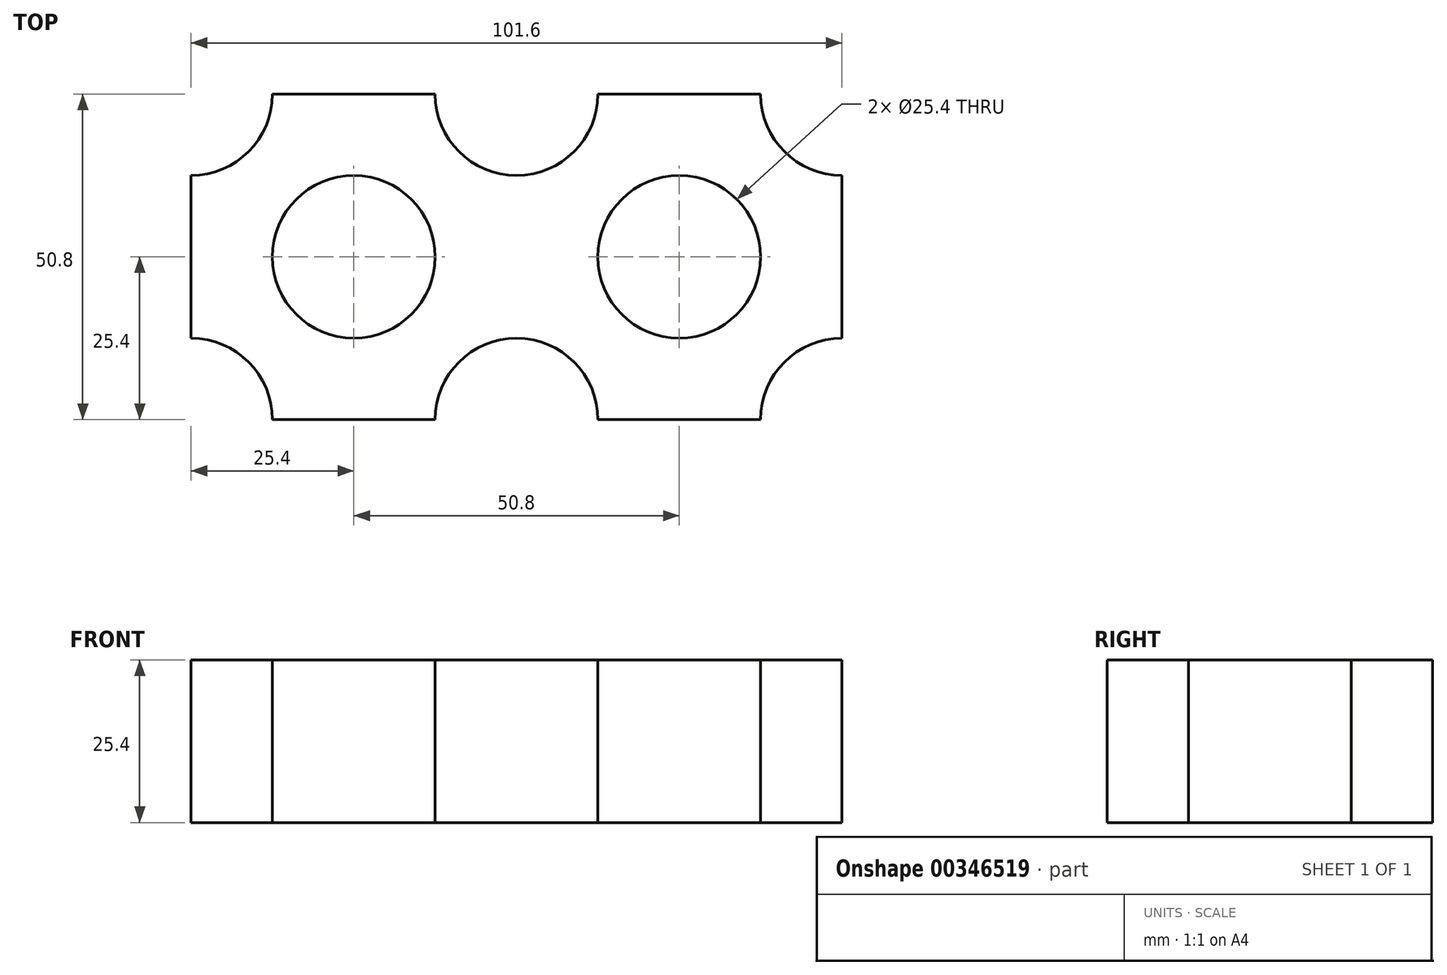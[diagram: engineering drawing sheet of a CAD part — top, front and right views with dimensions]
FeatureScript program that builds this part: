
annotation { "Feature Type Name" : "Feature", "Feature Type Description" : "" }
export const myFeature = defineFeature(function(context is Context, id is Id, definition is map)
    precondition{}
    {
        {
            var Q0;
            Q0=qCreatedBy(makeId("Top.planeOp"),FACE);
            var sketch = newSketch(context, id + "F0", { "sketchPlane" : qUnion([Q0])});
            skLineSegment(sketch, "E0", {"start": v(-50.8, 0) * mm, "end": v(-50.8, -12.7) * mm});
            skArc(sketch, "E1", {"start": v(-50.8, -12.7) * mm, "mid": v(-41.82, -16.42) * mm, "end": v(-38.1, -25.4) * mm});
            skLineSegment(sketch, "E2", {"start": v(-38.1, -25.4) * mm, "end": v(-12.7, -25.4) * mm});
            skArc(sketch, "E3", {"start": v(-12.7, -25.4) * mm, "mid": v(0, -12.7) * mm, "end": v(12.7, -25.4) * mm});
            skArc(sketch, "E4", {"start": v(38.1, -25.4) * mm, "mid": v(41.82, -16.42) * mm, "end": v(50.8, -12.7) * mm});
            skLineSegment(sketch, "E5", {"start": v(12.7, -25.4) * mm, "end": v(38.1, -25.4) * mm});
            skLineSegment(sketch, "E6", {"start": v(50.8, -12.7) * mm, "end": v(50.8, 0) * mm});
            skLineSegment(sketch, "E7", {"start": v(50.8, 0) * mm, "end": v(50.8, 12.7) * mm});
            skArc(sketch, "E8", {"start": v(50.8, 12.7) * mm, "mid": v(41.82, 16.42) * mm, "end": v(38.1, 25.4) * mm});
            skLineSegment(sketch, "E9", {"start": v(38.1, 25.4) * mm, "end": v(12.7, 25.4) * mm});
            skArc(sketch, "E10", {"start": v(12.7, 25.4) * mm, "mid": v(0, 12.7) * mm, "end": v(-12.7, 25.4) * mm});
            skArc(sketch, "E11", {"start": v(-38.1, 25.4) * mm, "mid": v(-41.82, 16.42) * mm, "end": v(-50.8, 12.7) * mm});
            skLineSegment(sketch, "E12", {"start": v(-12.7, 25.4) * mm, "end": v(-38.1, 25.4) * mm});
            skLineSegment(sketch, "E13", {"start": v(-50.8, 12.7) * mm, "end": v(-50.8, 0) * mm});
            skCircle(sketch, "E14", {"center": v(-25.4, 0) * mm, "radius": 12.7 * mm});
            skPoint(sketch, "E14.centerSnap0", {"position": v(-25.4, 25.4) * mm});
            skCircle(sketch, "E15", {"center": v(25.4, 0) * mm, "radius": 12.7 * mm});
            skPoint(sketch, "E15.centerSnap0", {"position": v(25.4, 25.4) * mm});
            skSolve(sketch);
        }
        {
            var Q0;
            Q0=makeQuery(id+"F0.imprint","IMPRINT",FACE,{"disambiguationData":[TD([[makeQuery(id+"F0.imprint","IMPRINT",EDGE,{"derivedFrom":sQuery(id+"F0.wireOp",EDGE,"E0")}),1.0]])]});
            extrude(context, id + "F1", {"entities" : qUnion([Q0]), "depth" : 25.4 * mm});
        }
    });
